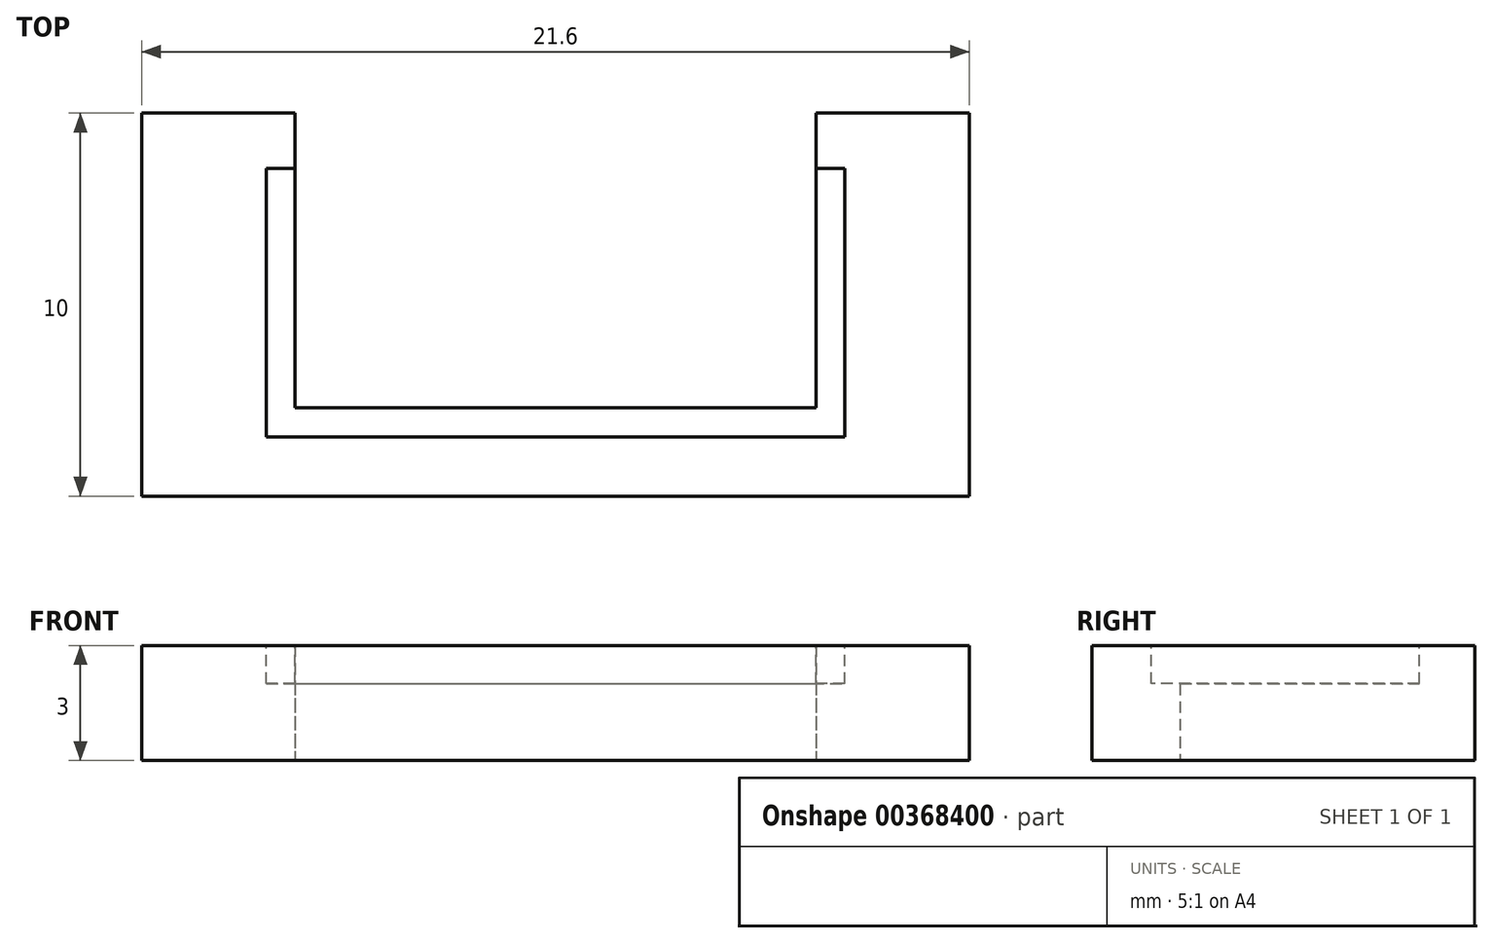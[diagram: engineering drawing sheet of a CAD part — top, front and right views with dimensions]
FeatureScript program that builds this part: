
annotation { "Feature Type Name" : "Feature", "Feature Type Description" : "" }
export const myFeature = defineFeature(function(context is Context, id is Id, definition is map)
    precondition{}
    {
        {
            var Q0;
            Q0=qCreatedBy(makeId("Top.planeOp"),FACE);
            var sketch = newSketch(context, id + "F0", { "sketchPlane" : qUnion([Q0])});
            skLineSegment(sketch, "E0.bottom", {"start": v(0, 0) * mm, "end": v(21.6, 0) * mm});
            skLineSegment(sketch, "E0.top", {"start": v(0, 10) * mm, "end": v(4, 10) * mm});
            skLineSegment(sketch, "E0.left", {"start": v(0, 0) * mm, "end": v(0, 10) * mm});
            skLineSegment(sketch, "E0.right", {"start": v(21.6, 10) * mm, "end": v(21.6, 0) * mm});
            skLineSegment(sketch, "E1", {"start": v(0, 5) * mm, "end": v(21.6, 5) * mm, "construction": true});
            skLineSegment(sketch, "E2", {"start": v(4, 2.3) * mm, "end": v(17.6, 2.3) * mm});
            skLineSegment(sketch, "E3", {"start": v(17.6, 2.3) * mm, "end": v(17.6, 10) * mm});
            skLineSegment(sketch, "E4", {"start": v(4, 2.3) * mm, "end": v(4, 10) * mm});
            skLineSegment(sketch, "E5.trimOffspring", {"start": v(17.6, 10) * mm, "end": v(21.6, 10) * mm});
            skSolve(sketch);
        }
        {
            var Q0;
            Q0=qSketchRegion(id+"F0",true);
            extrude(context, id + "F1", {"entities" : qUnion([Q0]), "depth" : 3 * mm});
        }
        {
            var Q0;
            Q0=makeQuery(id+"F1.opExtrude","CAP_FACE",FACE,{"disambiguationData":[OSD([sQuery(id+"F0.wireOp",EDGE,"E0.bottom"),sQuery(id+"F0.wireOp",EDGE,"E0.top"),sQuery(id+"F0.wireOp",EDGE,"E0.left"),sQuery(id+"F0.wireOp",EDGE,"E0.right"),sQuery(id+"F0.wireOp",EDGE,"E2"),sQuery(id+"F0.wireOp",EDGE,"E3"),sQuery(id+"F0.wireOp",EDGE,"E4"),sQuery(id+"F0.wireOp",EDGE,"E5.trimOffspring")])],"isStart":false});
            var sketch = newSketch(context, id + "F2", { "sketchPlane" : qUnion([Q0])});
            skLineSegment(sketch, "E6", {"start": v(4, 8.55) * mm, "end": v(3.25, 8.55) * mm});
            skLineSegment(sketch, "E7", {"start": v(3.25, 8.55) * mm, "end": v(3.25, 1.55) * mm});
            skLineSegment(sketch, "E8", {"start": v(3.25, 1.55) * mm, "end": v(18.35, 1.55) * mm});
            skLineSegment(sketch, "E9", {"start": v(18.35, 1.55) * mm, "end": v(18.35, 8.55) * mm});
            skLineSegment(sketch, "E10", {"start": v(18.35, 8.55) * mm, "end": v(17.6, 8.55) * mm});
            skLineSegment(sketch, "E11", {"start": v(17.6, 8.55) * mm, "end": v(17.6, 2.3) * mm});
            skLineSegment(sketch, "E12", {"start": v(17.6, 2.3) * mm, "end": v(4, 2.3) * mm});
            skLineSegment(sketch, "E13", {"start": v(4, 2.3) * mm, "end": v(4, 8.55) * mm});
            skSolve(sketch);
        }
        {
            var Q0;
            Q0=qSketchRegion(id+"F2",true);
            extrude(context, id + "F3", {"entities" : qUnion([Q0]), "operationType" : NewBodyOperationType.REMOVE, "oppositeDirection" : true, "depth" : 1 * mm});
        }
    });
